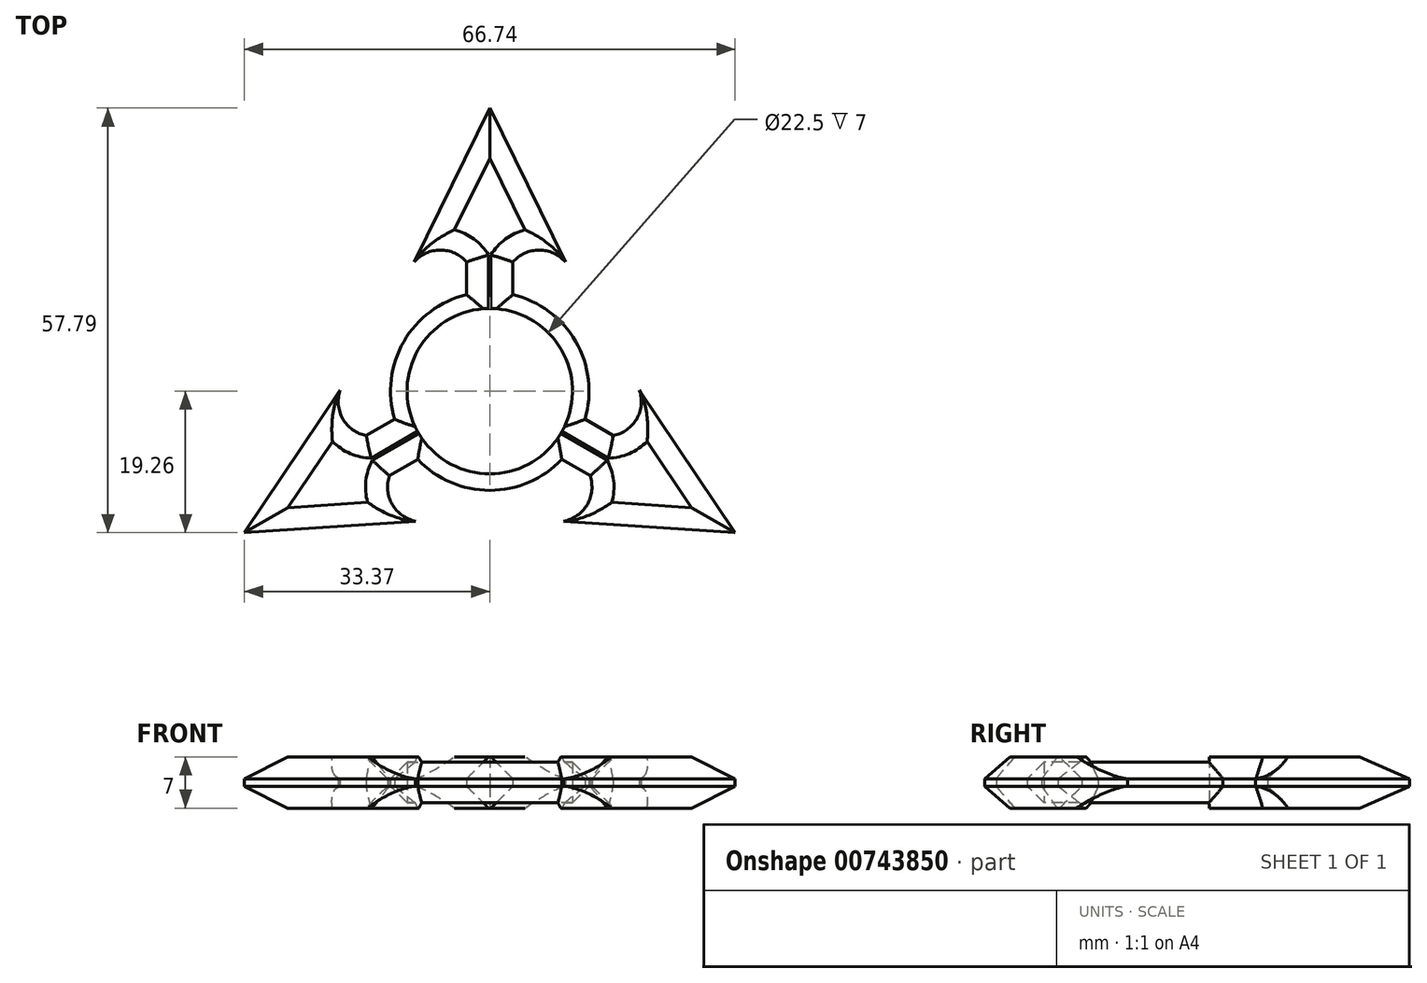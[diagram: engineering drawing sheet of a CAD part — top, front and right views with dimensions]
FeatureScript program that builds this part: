
annotation { "Feature Type Name" : "Feature", "Feature Type Description" : "" }
export const myFeature = defineFeature(function(context is Context, id is Id, definition is map)
    precondition{}
    {
        {
            var Q0;
            Q0=qCreatedBy(makeId("Top.planeOp"),FACE);
            var sketch = newSketch(context, id + "F0", { "sketchPlane" : qUnion([Q0])});
            skCircle(sketch, "E0", {"center": v(0, 0) * mm, "radius": 11.25 * mm});
            skCircle(sketch, "E1", {"center": v(0, 0) * mm, "radius": 13.5 * mm});
            skLineSegment(sketch, "E2", {"start": v(-3.15, 13.13) * mm, "end": v(-3.15, 17.57) * mm});
            skArc(sketch, "E3", {"start": v(-3.15, 17.57) * mm, "mid": v(-6.72, 19.2) * mm, "end": v(-10.28, 17.57) * mm});
            skLineSegment(sketch, "E4", {"start": v(-10.28, 17.57) * mm, "end": v(0, 38.53) * mm});
            skLineSegment(sketch, "E5.MirrorCS", {"start": v(10.28, 17.57) * mm, "end": v(0, 38.53) * mm});
            skArc(sketch, "E6.MirrorCS", {"start": v(3.15, 17.57) * mm, "mid": v(6.72, 19.2) * mm, "end": v(10.28, 17.57) * mm});
            skLineSegment(sketch, "E7.MirrorCS", {"start": v(3.15, 13.13) * mm, "end": v(3.15, 17.57) * mm});
            skLineSegment(sketch, "E8.1.0", {"start": v(-10.07, -17.69) * mm, "end": v(-33.37, -19.26) * mm});
            skArc(sketch, "E8.1.1", {"start": v(-13.64, -11.51) * mm, "mid": v(-13.27, -15.42) * mm, "end": v(-10.07, -17.69) * mm});
            skLineSegment(sketch, "E8.1.2", {"start": v(-9.8, -9.3) * mm, "end": v(-13.64, -11.51) * mm});
            skLineSegment(sketch, "E8.1.3", {"start": v(-12.94, -3.83) * mm, "end": v(-16.8, -6.05) * mm});
            skArc(sketch, "E8.1.4", {"start": v(-16.8, -6.05) * mm, "mid": v(-19.98, -3.78) * mm, "end": v(-20.35, 0.12) * mm});
            skLineSegment(sketch, "E8.1.5", {"start": v(-20.35, 0.12) * mm, "end": v(-33.37, -19.26) * mm});
            skLineSegment(sketch, "E8.2.0", {"start": v(20.35, 0.12) * mm, "end": v(33.37, -19.26) * mm});
            skArc(sketch, "E8.2.1", {"start": v(16.8, -6.05) * mm, "mid": v(19.98, -3.78) * mm, "end": v(20.35, 0.12) * mm});
            skLineSegment(sketch, "E8.2.2", {"start": v(12.94, -3.83) * mm, "end": v(16.8, -6.05) * mm});
            skLineSegment(sketch, "E8.2.3", {"start": v(9.8, -9.3) * mm, "end": v(13.64, -11.51) * mm});
            skArc(sketch, "E8.2.4", {"start": v(13.64, -11.51) * mm, "mid": v(13.27, -15.42) * mm, "end": v(10.07, -17.69) * mm});
            skLineSegment(sketch, "E8.2.5", {"start": v(10.07, -17.69) * mm, "end": v(33.37, -19.26) * mm});
            skSolve(sketch);
        }
        {
            var Q0;
            Q0=qSketchRegion(id+"F0",true);
            extrude(context, id + "F1", {"entities" : qUnion([Q0]), "depth" : 7 * mm, "offsetDistance" : 25 * mm});
        }
        {
            var Q0;
            Q0=makeQuery(id+"F1.opExtrude","CAP_EDGE",EDGE,{"disambiguationData":[OSD([sQuery(id+"F0.wireOp",EDGE,"E4")])],"isStart":false});
            var Q1;
            Q1=makeQuery(id+"F1.opExtrude","CAP_EDGE",EDGE,{"disambiguationData":[OSD([sQuery(id+"F0.wireOp",EDGE,"E3")])],"isStart":false});
            var Q2;
            Q2=makeQuery(id+"F1.opExtrude","CAP_EDGE",EDGE,{"disambiguationData":[OSD([sQuery(id+"F0.wireOp",EDGE,"E2")])],"isStart":false});
            var Q3;
            {var subQ0=sQuery(id+"F0.wireOp",EDGE,"E1");Q3=makeQuery(id+"F1.opExtrude","CAP_EDGE",EDGE,{"disambiguationData":[OSD([subQ0]),TDD([makeQuery(id+"F0.imprint","IMPRINT",EDGE,{"disambiguationData":[TD([[makeQuery(id+"F0.imprint","INTERSECT",VERTEX,{"derivedFrom":[subQ0,sQuery(id+"F0.wireOp",EDGE,"E2")]}),-1.0]])],"derivedFrom":subQ0})])],"isStart":false});}
            var Q4;
            Q4=makeQuery(id+"F1.opExtrude","CAP_EDGE",EDGE,{"disambiguationData":[OSD([sQuery(id+"F0.wireOp",EDGE,"E8.1.3")])],"isStart":false});
            var Q5;
            Q5=makeQuery(id+"F1.opExtrude","CAP_EDGE",EDGE,{"disambiguationData":[OSD([sQuery(id+"F0.wireOp",EDGE,"E8.1.4")])],"isStart":false});
            var Q6;
            Q6=makeQuery(id+"F1.opExtrude","CAP_EDGE",EDGE,{"disambiguationData":[OSD([sQuery(id+"F0.wireOp",EDGE,"E8.1.5")])],"isStart":false});
            var Q7;
            Q7=makeQuery(id+"F1.opExtrude","CAP_EDGE",EDGE,{"disambiguationData":[OSD([sQuery(id+"F0.wireOp",EDGE,"E8.1.0")])],"isStart":false});
            var Q8;
            Q8=makeQuery(id+"F1.opExtrude","CAP_EDGE",EDGE,{"disambiguationData":[OSD([sQuery(id+"F0.wireOp",EDGE,"E8.1.1")])],"isStart":false});
            var Q9;
            Q9=makeQuery(id+"F1.opExtrude","CAP_EDGE",EDGE,{"disambiguationData":[OSD([sQuery(id+"F0.wireOp",EDGE,"E8.1.2")])],"isStart":false});
            var Q10;
            {var subQ0=sQuery(id+"F0.wireOp",EDGE,"E1");Q10=makeQuery(id+"F1.opExtrude","CAP_EDGE",EDGE,{"disambiguationData":[OSD([subQ0]),TDD([makeQuery(id+"F0.imprint","IMPRINT",EDGE,{"disambiguationData":[TD([[makeQuery(id+"F0.imprint","INTERSECT",VERTEX,{"derivedFrom":[subQ0,sQuery(id+"F0.wireOp",EDGE,"E8.1.2")]}),-1.0]])],"derivedFrom":subQ0})])],"isStart":false});}
            var Q11;
            Q11=makeQuery(id+"F1.opExtrude","CAP_EDGE",EDGE,{"disambiguationData":[OSD([sQuery(id+"F0.wireOp",EDGE,"E8.2.3")])],"isStart":false});
            var Q12;
            Q12=makeQuery(id+"F1.opExtrude","CAP_EDGE",EDGE,{"disambiguationData":[OSD([sQuery(id+"F0.wireOp",EDGE,"E8.2.4")])],"isStart":false});
            var Q13;
            Q13=makeQuery(id+"F1.opExtrude","CAP_EDGE",EDGE,{"disambiguationData":[OSD([sQuery(id+"F0.wireOp",EDGE,"E8.2.5")])],"isStart":false});
            var Q14;
            Q14=makeQuery(id+"F1.opExtrude","CAP_EDGE",EDGE,{"disambiguationData":[OSD([sQuery(id+"F0.wireOp",EDGE,"E8.2.0")])],"isStart":false});
            var Q15;
            Q15=makeQuery(id+"F1.opExtrude","CAP_EDGE",EDGE,{"disambiguationData":[OSD([sQuery(id+"F0.wireOp",EDGE,"E8.2.1")])],"isStart":false});
            var Q16;
            Q16=makeQuery(id+"F1.opExtrude","CAP_EDGE",EDGE,{"disambiguationData":[OSD([sQuery(id+"F0.wireOp",EDGE,"E8.2.2")])],"isStart":false});
            var Q17;
            {var subQ0=sQuery(id+"F0.wireOp",EDGE,"E1");Q17=makeQuery(id+"F1.opExtrude","CAP_EDGE",EDGE,{"disambiguationData":[OSD([subQ0]),TDD([makeQuery(id+"F0.imprint","IMPRINT",EDGE,{"disambiguationData":[TD([[makeQuery(id+"F0.imprint","INTERSECT",VERTEX,{"derivedFrom":[subQ0,sQuery(id+"F0.wireOp",EDGE,"E7.MirrorCS")]}),1.0]])],"derivedFrom":subQ0})])],"isStart":false});}
            var Q18;
            Q18=makeQuery(id+"F1.opExtrude","CAP_EDGE",EDGE,{"disambiguationData":[OSD([sQuery(id+"F0.wireOp",EDGE,"E7.MirrorCS")])],"isStart":false});
            var Q19;
            Q19=makeQuery(id+"F1.opExtrude","CAP_EDGE",EDGE,{"disambiguationData":[OSD([sQuery(id+"F0.wireOp",EDGE,"E6.MirrorCS")])],"isStart":false});
            var Q20;
            Q20=makeQuery(id+"F1.opExtrude","CAP_EDGE",EDGE,{"disambiguationData":[OSD([sQuery(id+"F0.wireOp",EDGE,"E5.MirrorCS")])],"isStart":false});
            var Q21;
            Q21=makeQuery(id+"F1.opExtrude","CAP_EDGE",EDGE,{"disambiguationData":[OSD([sQuery(id+"F0.wireOp",EDGE,"E3")])],"isStart":true});
            var Q22;
            Q22=makeQuery(id+"F1.opExtrude","CAP_EDGE",EDGE,{"disambiguationData":[OSD([sQuery(id+"F0.wireOp",EDGE,"E4")])],"isStart":true});
            var Q23;
            Q23=makeQuery(id+"F1.opExtrude","CAP_EDGE",EDGE,{"disambiguationData":[OSD([sQuery(id+"F0.wireOp",EDGE,"E5.MirrorCS")])],"isStart":true});
            var Q24;
            Q24=makeQuery(id+"F1.opExtrude","CAP_EDGE",EDGE,{"disambiguationData":[OSD([sQuery(id+"F0.wireOp",EDGE,"E6.MirrorCS")])],"isStart":true});
            var Q25;
            Q25=makeQuery(id+"F1.opExtrude","CAP_EDGE",EDGE,{"disambiguationData":[OSD([sQuery(id+"F0.wireOp",EDGE,"E7.MirrorCS")])],"isStart":true});
            var Q26;
            {var subQ0=sQuery(id+"F0.wireOp",EDGE,"E1");Q26=makeQuery(id+"F1.opExtrude","CAP_EDGE",EDGE,{"disambiguationData":[OSD([subQ0]),TDD([makeQuery(id+"F0.imprint","IMPRINT",EDGE,{"disambiguationData":[TD([[makeQuery(id+"F0.imprint","INTERSECT",VERTEX,{"derivedFrom":[subQ0,sQuery(id+"F0.wireOp",EDGE,"E7.MirrorCS")]}),1.0]])],"derivedFrom":subQ0})])],"isStart":true});}
            var Q27;
            Q27=makeQuery(id+"F1.opExtrude","CAP_EDGE",EDGE,{"disambiguationData":[OSD([sQuery(id+"F0.wireOp",EDGE,"E8.2.2")])],"isStart":true});
            var Q28;
            Q28=makeQuery(id+"F1.opExtrude","CAP_EDGE",EDGE,{"disambiguationData":[OSD([sQuery(id+"F0.wireOp",EDGE,"E8.2.1")])],"isStart":true});
            var Q29;
            Q29=makeQuery(id+"F1.opExtrude","CAP_EDGE",EDGE,{"disambiguationData":[OSD([sQuery(id+"F0.wireOp",EDGE,"E8.2.0")])],"isStart":true});
            var Q30;
            Q30=makeQuery(id+"F1.opExtrude","CAP_EDGE",EDGE,{"disambiguationData":[OSD([sQuery(id+"F0.wireOp",EDGE,"E8.2.5")])],"isStart":true});
            var Q31;
            Q31=makeQuery(id+"F1.opExtrude","CAP_EDGE",EDGE,{"disambiguationData":[OSD([sQuery(id+"F0.wireOp",EDGE,"E8.2.4")])],"isStart":true});
            var Q32;
            Q32=makeQuery(id+"F1.opExtrude","CAP_EDGE",EDGE,{"disambiguationData":[OSD([sQuery(id+"F0.wireOp",EDGE,"E8.2.3")])],"isStart":true});
            var Q33;
            {var subQ0=sQuery(id+"F0.wireOp",EDGE,"E1");Q33=makeQuery(id+"F1.opExtrude","CAP_EDGE",EDGE,{"disambiguationData":[OSD([subQ0]),TDD([makeQuery(id+"F0.imprint","IMPRINT",EDGE,{"disambiguationData":[TD([[makeQuery(id+"F0.imprint","INTERSECT",VERTEX,{"derivedFrom":[subQ0,sQuery(id+"F0.wireOp",EDGE,"E8.1.2")]}),-1.0]])],"derivedFrom":subQ0})])],"isStart":true});}
            var Q34;
            Q34=makeQuery(id+"F1.opExtrude","CAP_EDGE",EDGE,{"disambiguationData":[OSD([sQuery(id+"F0.wireOp",EDGE,"E8.1.2")])],"isStart":true});
            var Q35;
            Q35=makeQuery(id+"F1.opExtrude","CAP_EDGE",EDGE,{"disambiguationData":[OSD([sQuery(id+"F0.wireOp",EDGE,"E8.1.1")])],"isStart":true});
            var Q36;
            Q36=makeQuery(id+"F1.opExtrude","CAP_EDGE",EDGE,{"disambiguationData":[OSD([sQuery(id+"F0.wireOp",EDGE,"E8.1.0")])],"isStart":true});
            var Q37;
            Q37=makeQuery(id+"F1.opExtrude","CAP_EDGE",EDGE,{"disambiguationData":[OSD([sQuery(id+"F0.wireOp",EDGE,"E8.1.5")])],"isStart":true});
            var Q38;
            Q38=makeQuery(id+"F1.opExtrude","CAP_EDGE",EDGE,{"disambiguationData":[OSD([sQuery(id+"F0.wireOp",EDGE,"E8.1.4")])],"isStart":true});
            var Q39;
            Q39=makeQuery(id+"F1.opExtrude","CAP_EDGE",EDGE,{"disambiguationData":[OSD([sQuery(id+"F0.wireOp",EDGE,"E8.1.3")])],"isStart":true});
            var Q40;
            {var subQ0=sQuery(id+"F0.wireOp",EDGE,"E1");Q40=makeQuery(id+"F1.opExtrude","CAP_EDGE",EDGE,{"disambiguationData":[OSD([subQ0]),TDD([makeQuery(id+"F0.imprint","IMPRINT",EDGE,{"disambiguationData":[TD([[makeQuery(id+"F0.imprint","INTERSECT",VERTEX,{"derivedFrom":[subQ0,sQuery(id+"F0.wireOp",EDGE,"E2")]}),-1.0]])],"derivedFrom":subQ0})])],"isStart":true});}
            var Q41;
            Q41=makeQuery(id+"F1.opExtrude","CAP_EDGE",EDGE,{"disambiguationData":[OSD([sQuery(id+"F0.wireOp",EDGE,"E2")])],"isStart":true});
            chamfer(context, id + "F2", {"entities" : qUnion([Q0, Q1, Q2, Q3, Q4, Q5, Q6, Q7, Q8, Q9, Q10, Q11, Q12, Q13, Q14, Q15, Q16, Q17, Q18, Q19, Q20, Q21, Q22, Q23, Q24, Q25, Q26, Q27, Q28, Q29, Q30, Q31, Q32, Q33, Q34, Q35, Q36, Q37, Q38, Q39, Q40, Q41]), "width" : 3 * mm, "tangentPropagation" : true});
        }
    });
